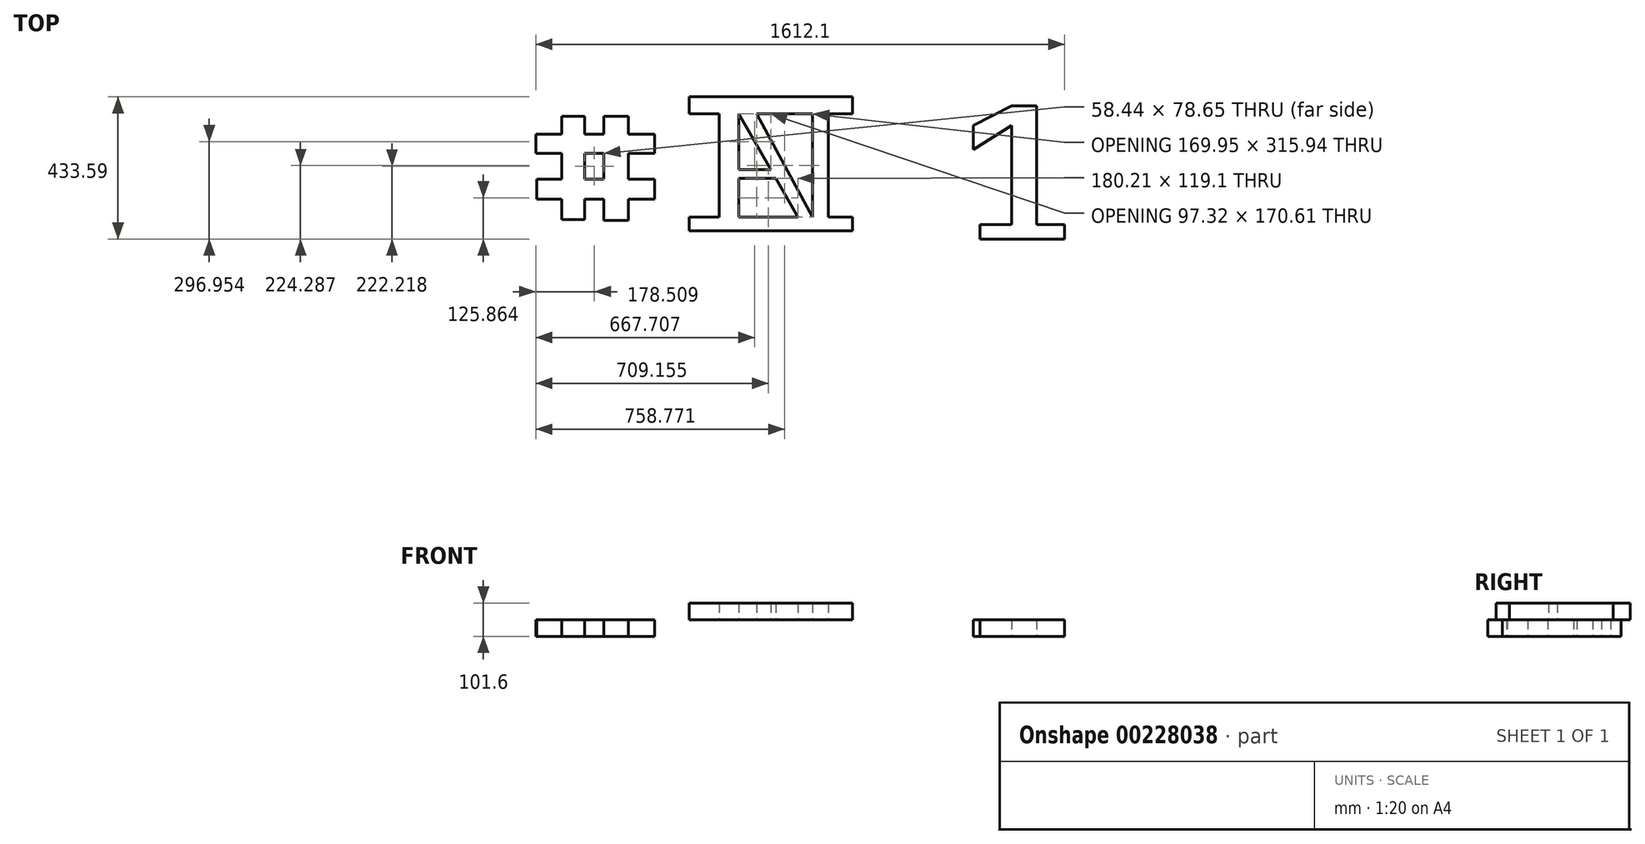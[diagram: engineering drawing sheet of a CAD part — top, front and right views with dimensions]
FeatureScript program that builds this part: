
annotation { "Feature Type Name" : "Feature", "Feature Type Description" : "" }
export const myFeature = defineFeature(function(context is Context, id is Id, definition is map)
    precondition{}
    {
        {
            var Q0;
            Q0=qCreatedBy(makeId("Top.planeOp"),FACE);
            var sketch = newSketch(context, id + "F0", { "sketchPlane" : qUnion([Q0])});
            skLineSegment(sketch, "E0.bottom", {"start": v(-405.86, 86.86) * mm, "end": v(317.28, 86.86) * mm});
            skLineSegment(sketch, "E0.top", {"start": v(-405.86, 35.53) * mm, "end": v(317.28, 35.53) * mm});
            skLineSegment(sketch, "E0.left", {"start": v(-405.86, 86.86) * mm, "end": v(-405.86, 35.53) * mm});
            skLineSegment(sketch, "E0.right", {"start": v(317.28, 86.86) * mm, "end": v(317.28, 35.53) * mm});
            skLineSegment(sketch, "E1.bottom", {"start": v(-313.47, 35.53) * mm, "end": v(-254.16, 35.53) * mm});
            skLineSegment(sketch, "E1.top", {"start": v(-313.47, -280.42) * mm, "end": v(-254.16, -280.42) * mm});
            skLineSegment(sketch, "E1.left", {"start": v(-313.47, 35.53) * mm, "end": v(-313.47, -280.42) * mm});
            skLineSegment(sketch, "E1.right", {"start": v(-254.16, 35.53) * mm, "end": v(-254.16, -280.42) * mm});
            skLineSegment(sketch, "E2.bottom", {"start": v(-405.86, -280.42) * mm, "end": v(329.82, -280.42) * mm});
            skLineSegment(sketch, "E2.top", {"start": v(-405.86, -321.48) * mm, "end": v(329.82, -321.48) * mm});
            skLineSegment(sketch, "E2.left", {"start": v(-405.86, -280.42) * mm, "end": v(-405.86, -321.48) * mm});
            skLineSegment(sketch, "E2.right", {"start": v(329.82, -280.42) * mm, "end": v(329.82, -321.48) * mm});
            skSolve(sketch);
        }
        {
            var Q0;
            Q0 = qSketchRegion(id + "F0", true);
            extrude(context, id + "F1", {"entities" : qUnion([Q0]), "depth" : 50.8 * mm});
        }
        {
            var Q0;
            Q0=makeQuery(id+"F1.opExtrude","CAP_FACE",FACE,{"disambiguationData":[OSD([sQuery(id+"F0.wireOp",EDGE,"E0.bottom"),sQuery(id+"F0.wireOp",EDGE,"E0.top"),sQuery(id+"F0.wireOp",EDGE,"E0.left"),sQuery(id+"F0.wireOp",EDGE,"E0.right"),sQuery(id+"F0.wireOp",EDGE,"E1.left"),sQuery(id+"F0.wireOp",EDGE,"E1.right"),sQuery(id+"F0.wireOp",EDGE,"E2.bottom"),sQuery(id+"F0.wireOp",EDGE,"E2.top"),sQuery(id+"F0.wireOp",EDGE,"E2.left"),sQuery(id+"F0.wireOp",EDGE,"E2.right")])],"isStart":false});
            var sketch = newSketch(context, id + "F2", { "sketchPlane" : qUnion([Q0])});
            skLineSegment(sketch, "E3", {"start": v(-254.16, 35.53) * mm, "end": v(-73.95, -280.42) * mm});
            skLineSegment(sketch, "E4", {"start": v(-199.41, 35.53) * mm, "end": v(-29.46, -280.42) * mm});
            skLineSegment(sketch, "E5.bottom", {"start": v(-29.46, -280.42) * mm, "end": v(18.44, -280.42) * mm});
            skLineSegment(sketch, "E5.top", {"start": v(-29.46, 35.53) * mm, "end": v(18.44, 35.53) * mm});
            skLineSegment(sketch, "E5.left", {"start": v(-29.46, -280.42) * mm, "end": v(-29.46, 35.53) * mm});
            skLineSegment(sketch, "E5.right", {"start": v(18.44, -280.42) * mm, "end": v(18.44, 35.53) * mm});
            skLineSegment(sketch, "E6", {"start": v(-254.16, -135.08) * mm, "end": v(-156.84, -135.08) * mm});
            skLineSegment(sketch, "E7", {"start": v(-254.16, -161.32) * mm, "end": v(-141.88, -161.32) * mm});
            skSolve(sketch);
        }
        {
            var Q0;
            {var subQ0=sQuery(id+"F2.wireOp",EDGE,"E6");Q0=makeQuery(id+"F2.imprint","IMPRINT",FACE,{"disambiguationData":[TD([[makeQuery(id+"F2.imprint","IMPRINT",EDGE,{"derivedFrom":subQ0}),-1.0]])]});}
            var Q1;
            {var subQ0=sQuery(id+"F2.wireOp",EDGE,"E4");Q1=makeQuery(id+"F2.imprint","IMPRINT",FACE,{"disambiguationData":[TD([[makeQuery(id+"F2.imprint","IMPRINT",EDGE,{"derivedFrom":subQ0}),-1.0]])]});}
            var Q2;
            Q2=makeQuery(id+"F2.imprint","IMPRINT",FACE,{"disambiguationData":[TD([[makeQuery(id+"F2.imprint","IMPRINT",EDGE,{"derivedFrom":sQuery(id+"F2.wireOp",EDGE,"E5.bottom")}),1.0]])]});
            extrude(context, id + "F3", {"entities" : qUnion([Q0, Q1, Q2]), "operationType" : NewBodyOperationType.ADD, "oppositeDirection" : true, "depth" : 2.54 * mm});
        }
        {
            var Q0;
            Q0=makeQuery(id+"F3.opExtrude","CAP_FACE",FACE,{"disambiguationData":[OSD([sQuery(id+"F2.wireOp",EDGE,"E5.bottom"),sQuery(id+"F2.wireOp",EDGE,"E5.top"),sQuery(id+"F2.wireOp",EDGE,"E5.left"),sQuery(id+"F2.wireOp",EDGE,"E5.right")])],"isStart":false});
            var Q1;
            {var subQ0=sQuery(id+"F0.wireOp",EDGE,"E2.bottom");var subQ1=sQuery(id+"F0.wireOp",EDGE,"E1.right");var subQ2=sQuery(id+"F0.wireOp",EDGE,"E0.top");Q1=makeQuery(id+"F3.boolean.opBoolean","MERGE",FACE,{"derivedFrom":[makeQuery(id+"F1.opExtrude","CAP_FACE",FACE,{"disambiguationData":[OSD([sQuery(id+"F0.wireOp",EDGE,"E0.bottom"),subQ2,sQuery(id+"F0.wireOp",EDGE,"E0.left"),sQuery(id+"F0.wireOp",EDGE,"E0.right"),sQuery(id+"F0.wireOp",EDGE,"E1.left"),subQ1,subQ0,sQuery(id+"F0.wireOp",EDGE,"E2.top"),sQuery(id+"F0.wireOp",EDGE,"E2.left"),sQuery(id+"F0.wireOp",EDGE,"E2.right")])],"isStart":false}),makeQuery(id+"F3.opExtrude","CAP_FACE",FACE,{"disambiguationData":[OSD([subQ2,subQ1,subQ0,sQuery(id+"F2.wireOp",EDGE,"E3"),sQuery(id+"F2.wireOp",EDGE,"E4"),sQuery(id+"F2.wireOp",EDGE,"E6"),sQuery(id+"F2.wireOp",EDGE,"E7")])],"isStart":true}),makeQuery(id+"F3.opExtrude","CAP_FACE",FACE,{"disambiguationData":[OSD([sQuery(id+"F2.wireOp",EDGE,"E5.bottom"),sQuery(id+"F2.wireOp",EDGE,"E5.top"),sQuery(id+"F2.wireOp",EDGE,"E5.left"),sQuery(id+"F2.wireOp",EDGE,"E5.right")])],"isStart":true})]});}
            extrude(context, id + "F4", {"entities" : qUnion([Q0, Q1]), "operationType" : NewBodyOperationType.ADD, "depth" : 50.8 * mm});
        }
        {
            var Q0;
            Q0=qCreatedBy(makeId("Top.planeOp"),FACE);
            var sketch = newSketch(context, id + "F5", { "sketchPlane" : qUnion([Q0])});
            skLineSegment(sketch, "E8.bottom", {"start": v(-665.48, 27.15) * mm, "end": v(-590.63, 27.15) * mm});
            skLineSegment(sketch, "E8.top", {"start": v(-665.48, -289.47) * mm, "end": v(-590.63, -289.47) * mm});
            skLineSegment(sketch, "E8.left", {"start": v(-665.48, 27.15) * mm, "end": v(-665.48, -289.47) * mm});
            skLineSegment(sketch, "E8.right", {"start": v(-590.63, 27.15) * mm, "end": v(-590.63, -289.47) * mm});
            skLineSegment(sketch, "E9.bottom", {"start": v(-723.92, 27.15) * mm, "end": v(-793.68, 27.15) * mm});
            skLineSegment(sketch, "E9.top", {"start": v(-723.92, -287.13) * mm, "end": v(-793.68, -287.13) * mm});
            skLineSegment(sketch, "E9.left", {"start": v(-723.92, 27.15) * mm, "end": v(-723.92, -287.13) * mm});
            skLineSegment(sketch, "E9.right", {"start": v(-793.68, 27.15) * mm, "end": v(-793.68, -287.13) * mm});
            skLineSegment(sketch, "E10.bottom", {"start": v(-873.2, -27.09) * mm, "end": v(-510.93, -27.09) * mm});
            skLineSegment(sketch, "E10.top", {"start": v(-873.2, -85.19) * mm, "end": v(-510.93, -85.19) * mm});
            skLineSegment(sketch, "E10.left", {"start": v(-873.2, -27.09) * mm, "end": v(-873.2, -85.19) * mm});
            skLineSegment(sketch, "E10.right", {"start": v(-510.93, -27.09) * mm, "end": v(-510.93, -85.19) * mm});
            skLineSegment(sketch, "E11.bottom", {"start": v(-870.22, -163.84) * mm, "end": v(-510.93, -163.84) * mm});
            skLineSegment(sketch, "E11.top", {"start": v(-870.22, -224.98) * mm, "end": v(-510.93, -224.98) * mm});
            skLineSegment(sketch, "E11.left", {"start": v(-870.22, -163.84) * mm, "end": v(-870.22, -224.98) * mm});
            skLineSegment(sketch, "E11.right", {"start": v(-510.93, -163.84) * mm, "end": v(-510.93, -224.98) * mm});
            skSolve(sketch);
        }
        {
            var Q0;
            {var subQ0=sQuery(id+"F5.wireOp",EDGE,"E9.bottom");Q0=makeQuery(id+"F5.imprint","IMPRINT",FACE,{"disambiguationData":[TD([[makeQuery(id+"F5.imprint","IMPRINT",EDGE,{"derivedFrom":subQ0}),1.0]])]});}
            var Q1;
            {var subQ0=sQuery(id+"F5.wireOp",EDGE,"E10.bottom");var subQ1=sQuery(id+"F5.wireOp",EDGE,"E9.left");var subQ2=makeQuery(id+"F5.imprint","INTERSECT",VERTEX,{"derivedFrom":[subQ1,subQ0]});Q1=makeQuery(id+"F5.imprint","IMPRINT",FACE,{"disambiguationData":[TD([[makeQuery(id+"F5.imprint","IMPRINT",EDGE,{"disambiguationData":[TD([[subQ2,-1.0]])],"derivedFrom":subQ1}),-1.0]])]});}
            var Q2;
            {var subQ5=sQuery(id+"F5.wireOp",EDGE,"E10.left");Q2=makeQuery(id+"F5.imprint","IMPRINT",FACE,{"disambiguationData":[TD([[makeQuery(id+"F5.imprint","IMPRINT",EDGE,{"derivedFrom":subQ5}),1.0]])]});}
            var Q3;
            {var subQ0=sQuery(id+"F5.wireOp",EDGE,"E10.bottom");var subQ1=sQuery(id+"F5.wireOp",EDGE,"E8.left");var subQ2=makeQuery(id+"F5.imprint","INTERSECT",VERTEX,{"derivedFrom":[subQ1,subQ0]});Q3=makeQuery(id+"F5.imprint","IMPRINT",FACE,{"disambiguationData":[TD([[makeQuery(id+"F5.imprint","IMPRINT",EDGE,{"disambiguationData":[TD([[subQ2,-1.0]])],"derivedFrom":subQ1}),1.0]])]});}
            var Q4;
            {var subQ0=sQuery(id+"F5.wireOp",EDGE,"E8.bottom");Q4=makeQuery(id+"F5.imprint","IMPRINT",FACE,{"disambiguationData":[TD([[makeQuery(id+"F5.imprint","IMPRINT",EDGE,{"derivedFrom":subQ0}),-1.0]])]});}
            var Q5;
            {var subQ0=sQuery(id+"F5.wireOp",EDGE,"E10.bottom");var subQ1=sQuery(id+"F5.wireOp",EDGE,"E8.left");var subQ2=makeQuery(id+"F5.imprint","INTERSECT",VERTEX,{"derivedFrom":[subQ1,subQ0]});Q5=makeQuery(id+"F5.imprint","IMPRINT",FACE,{"disambiguationData":[TD([[makeQuery(id+"F5.imprint","IMPRINT",EDGE,{"disambiguationData":[TD([[subQ2,-1.0]])],"derivedFrom":subQ1}),-1.0]])]});}
            var Q6;
            {var subQ5=sQuery(id+"F5.wireOp",EDGE,"E10.right");Q6=makeQuery(id+"F5.imprint","IMPRINT",FACE,{"disambiguationData":[TD([[makeQuery(id+"F5.imprint","IMPRINT",EDGE,{"derivedFrom":subQ5}),-1.0]])]});}
            var Q7;
            {var subQ0=sQuery(id+"F5.wireOp",EDGE,"E10.top");var subQ1=sQuery(id+"F5.wireOp",EDGE,"E8.left");var subQ2=makeQuery(id+"F5.imprint","INTERSECT",VERTEX,{"derivedFrom":[subQ1,subQ0]});Q7=makeQuery(id+"F5.imprint","IMPRINT",FACE,{"disambiguationData":[TD([[makeQuery(id+"F5.imprint","IMPRINT",EDGE,{"disambiguationData":[TD([[subQ2,-1.0]])],"derivedFrom":subQ1}),1.0]])]});}
            var Q8;
            {var subQ0=sQuery(id+"F5.wireOp",EDGE,"E11.top");var subQ1=sQuery(id+"F5.wireOp",EDGE,"E8.left");var subQ2=makeQuery(id+"F5.imprint","INTERSECT",VERTEX,{"derivedFrom":[subQ1,subQ0]});Q8=makeQuery(id+"F5.imprint","IMPRINT",FACE,{"disambiguationData":[TD([[makeQuery(id+"F5.imprint","IMPRINT",EDGE,{"disambiguationData":[TD([[subQ2,1.0]])],"derivedFrom":subQ1}),1.0]])]});}
            var Q9;
            {var subQ5=sQuery(id+"F5.wireOp",EDGE,"E11.right");Q9=makeQuery(id+"F5.imprint","IMPRINT",FACE,{"disambiguationData":[TD([[makeQuery(id+"F5.imprint","IMPRINT",EDGE,{"derivedFrom":subQ5}),-1.0]])]});}
            var Q10;
            {var subQ0=sQuery(id+"F5.wireOp",EDGE,"E8.top");Q10=makeQuery(id+"F5.imprint","IMPRINT",FACE,{"disambiguationData":[TD([[makeQuery(id+"F5.imprint","IMPRINT",EDGE,{"derivedFrom":subQ0}),1.0]])]});}
            var Q11;
            {var subQ0=sQuery(id+"F5.wireOp",EDGE,"E11.top");var subQ1=sQuery(id+"F5.wireOp",EDGE,"E8.left");var subQ2=makeQuery(id+"F5.imprint","INTERSECT",VERTEX,{"derivedFrom":[subQ1,subQ0]});Q11=makeQuery(id+"F5.imprint","IMPRINT",FACE,{"disambiguationData":[TD([[makeQuery(id+"F5.imprint","IMPRINT",EDGE,{"disambiguationData":[TD([[subQ2,1.0]])],"derivedFrom":subQ1}),-1.0]])]});}
            var Q12;
            {var subQ0=sQuery(id+"F5.wireOp",EDGE,"E9.top");Q12=makeQuery(id+"F5.imprint","IMPRINT",FACE,{"disambiguationData":[TD([[makeQuery(id+"F5.imprint","IMPRINT",EDGE,{"derivedFrom":subQ0}),-1.0]])]});}
            var Q13;
            {var subQ0=sQuery(id+"F5.wireOp",EDGE,"E11.top");var subQ1=sQuery(id+"F5.wireOp",EDGE,"E9.left");var subQ2=makeQuery(id+"F5.imprint","INTERSECT",VERTEX,{"derivedFrom":[subQ1,subQ0]});Q13=makeQuery(id+"F5.imprint","IMPRINT",FACE,{"disambiguationData":[TD([[makeQuery(id+"F5.imprint","IMPRINT",EDGE,{"disambiguationData":[TD([[subQ2,1.0]])],"derivedFrom":subQ1}),-1.0]])]});}
            var Q14;
            {var subQ5=sQuery(id+"F5.wireOp",EDGE,"E11.left");Q14=makeQuery(id+"F5.imprint","IMPRINT",FACE,{"disambiguationData":[TD([[makeQuery(id+"F5.imprint","IMPRINT",EDGE,{"derivedFrom":subQ5}),1.0]])]});}
            var Q15;
            {var subQ0=sQuery(id+"F5.wireOp",EDGE,"E10.top");var subQ1=sQuery(id+"F5.wireOp",EDGE,"E9.left");var subQ2=makeQuery(id+"F5.imprint","INTERSECT",VERTEX,{"derivedFrom":[subQ1,subQ0]});Q15=makeQuery(id+"F5.imprint","IMPRINT",FACE,{"disambiguationData":[TD([[makeQuery(id+"F5.imprint","IMPRINT",EDGE,{"disambiguationData":[TD([[subQ2,-1.0]])],"derivedFrom":subQ1}),-1.0]])]});}
            extrude(context, id + "F6", {"entities" : qUnion([Q0, Q1, Q2, Q3, Q4, Q5, Q6, Q7, Q8, Q9, Q10, Q11, Q12, Q13, Q14, Q15]), "depth" : 50.8 * mm});
        }
        {
            var Q0;
            Q0=qCreatedBy(makeId("Top.planeOp"),FACE);
            var sketch = newSketch(context, id + "F7", { "sketchPlane" : qUnion([Q0])});
            skLineSegment(sketch, "E12.bottom", {"start": v(577.8, 59.58) * mm, "end": v(654.22, 59.58) * mm});
            skLineSegment(sketch, "E12.top", {"start": v(577.8, -302.56) * mm, "end": v(654.22, -302.56) * mm});
            skLineSegment(sketch, "E12.left", {"start": v(577.8, 59.58) * mm, "end": v(577.8, -302.56) * mm});
            skLineSegment(sketch, "E12.right", {"start": v(654.22, 59.58) * mm, "end": v(654.22, -302.56) * mm});
            skPoint(sketch, "E13.firstSnap0", {"position": v(616.01, -302.56) * mm});
            skLineSegment(sketch, "E13.bottom", {"start": v(481.03, -302.56) * mm, "end": v(738.89, -302.56) * mm});
            skLineSegment(sketch, "E13.top", {"start": v(481.03, -346.73) * mm, "end": v(738.89, -346.73) * mm});
            skLineSegment(sketch, "E13.left", {"start": v(481.03, -302.56) * mm, "end": v(481.03, -346.73) * mm});
            skLineSegment(sketch, "E13.right", {"start": v(738.89, -302.56) * mm, "end": v(738.89, -346.73) * mm});
            skLineSegment(sketch, "E14", {"start": v(461.14, 0) * mm, "end": v(577.8, 59.58) * mm});
            skLineSegment(sketch, "E15", {"start": v(461.14, 0) * mm, "end": v(461.14, -74.55) * mm});
            skLineSegment(sketch, "E16", {"start": v(461.14, -74.55) * mm, "end": v(577.8, 0) * mm});
            skSolve(sketch);
        }
        {
            var Q0;
            {var subQ5=sQuery(id+"F7.wireOp",EDGE,"E12.bottom");Q0=makeQuery(id+"F7.imprint","IMPRINT",FACE,{"disambiguationData":[TD([[makeQuery(id+"F7.imprint","IMPRINT",EDGE,{"derivedFrom":subQ5}),-1.0]])]});}
            var Q1;
            Q1=makeQuery(id+"F7.imprint","IMPRINT",FACE,{"disambiguationData":[TD([[makeQuery(id+"F7.imprint","IMPRINT",EDGE,{"derivedFrom":sQuery(id+"F7.wireOp",EDGE,"E13.top")}),1.0]])]});
            var Q2;
            {var subQ0=sQuery(id+"F7.wireOp",EDGE,"E14");Q2=makeQuery(id+"F7.imprint","IMPRINT",FACE,{"disambiguationData":[TD([[makeQuery(id+"F7.imprint","IMPRINT",EDGE,{"derivedFrom":subQ0}),-1.0]])]});}
            extrude(context, id + "F8", {"entities" : qUnion([Q0, Q1, Q2]), "depth" : 50.8 * mm});
        }
        {
            var Q0;
            {var subQ0=sQuery(id+"F0.wireOp",EDGE,"E2.bottom");var subQ1=sQuery(id+"F0.wireOp",EDGE,"E1.right");var subQ2=sQuery(id+"F0.wireOp",EDGE,"E0.top");Q0=makeQuery(id+"F3.boolean.opBoolean","MERGE",FACE,{"derivedFrom":[makeQuery(id+"F1.opExtrude","CAP_FACE",FACE,{"disambiguationData":[OSD([sQuery(id+"F0.wireOp",EDGE,"E0.bottom"),subQ2,sQuery(id+"F0.wireOp",EDGE,"E0.left"),sQuery(id+"F0.wireOp",EDGE,"E0.right"),sQuery(id+"F0.wireOp",EDGE,"E1.left"),subQ1,subQ0,sQuery(id+"F0.wireOp",EDGE,"E2.top"),sQuery(id+"F0.wireOp",EDGE,"E2.left"),sQuery(id+"F0.wireOp",EDGE,"E2.right")])],"isStart":false}),makeQuery(id+"F3.opExtrude","CAP_FACE",FACE,{"disambiguationData":[OSD([subQ2,subQ1,subQ0,sQuery(id+"F2.wireOp",EDGE,"E3"),sQuery(id+"F2.wireOp",EDGE,"E4"),sQuery(id+"F2.wireOp",EDGE,"E6"),sQuery(id+"F2.wireOp",EDGE,"E7")])],"isStart":true}),makeQuery(id+"F3.opExtrude","CAP_FACE",FACE,{"disambiguationData":[OSD([sQuery(id+"F2.wireOp",EDGE,"E5.bottom"),sQuery(id+"F2.wireOp",EDGE,"E5.top"),sQuery(id+"F2.wireOp",EDGE,"E5.left"),sQuery(id+"F2.wireOp",EDGE,"E5.right")])],"isStart":true})]});}
            var sketch = newSketch(context, id + "F9", { "sketchPlane" : qUnion([Q0])});
            skLineSegment(sketch, "E17", {"start": v(92.53, 86.86) * mm, "end": v(92.53, -321.48) * mm});
            skSolve(sketch);
        }
        {
            var Q0;
            Q0=makeQuery(id+"F1.opExtrude","SWEPT_BODY",BODY,{"disambiguationData":[OSD([sQuery(id+"F0.wireOp",EDGE,"E0.bottom"),sQuery(id+"F0.wireOp",EDGE,"E0.top"),sQuery(id+"F0.wireOp",EDGE,"E0.left"),sQuery(id+"F0.wireOp",EDGE,"E0.right"),sQuery(id+"F0.wireOp",EDGE,"E1.left"),sQuery(id+"F0.wireOp",EDGE,"E1.right"),sQuery(id+"F0.wireOp",EDGE,"E2.bottom"),sQuery(id+"F0.wireOp",EDGE,"E2.top"),sQuery(id+"F0.wireOp",EDGE,"E2.left"),sQuery(id+"F0.wireOp",EDGE,"E2.right")])]});
            deleteBodies(context, id + "F10", {"entities" : qUnion([Q0])});
        }
        {
            var Q0;
            {var subQ23=sQuery(id+"F0.wireOp",EDGE,"E0.left");var subQ29=makeQuery(id+"F1.opExtrude","CAP_EDGE",EDGE,{"disambiguationData":[OSD([subQ23])],"isStart":false});Q0=makeQuery(id+"F9.imprint","IMPRINT",FACE,{"disambiguationData":[TD([[makeQuery(id+"F9.imprint","IMPRINT",EDGE,{"derivedFrom":subQ29}),1.0]])]});}
            extrude(context, id + "F11", {"entities" : qUnion([Q0]), "depth" : 50.8 * mm});
        }
    });
